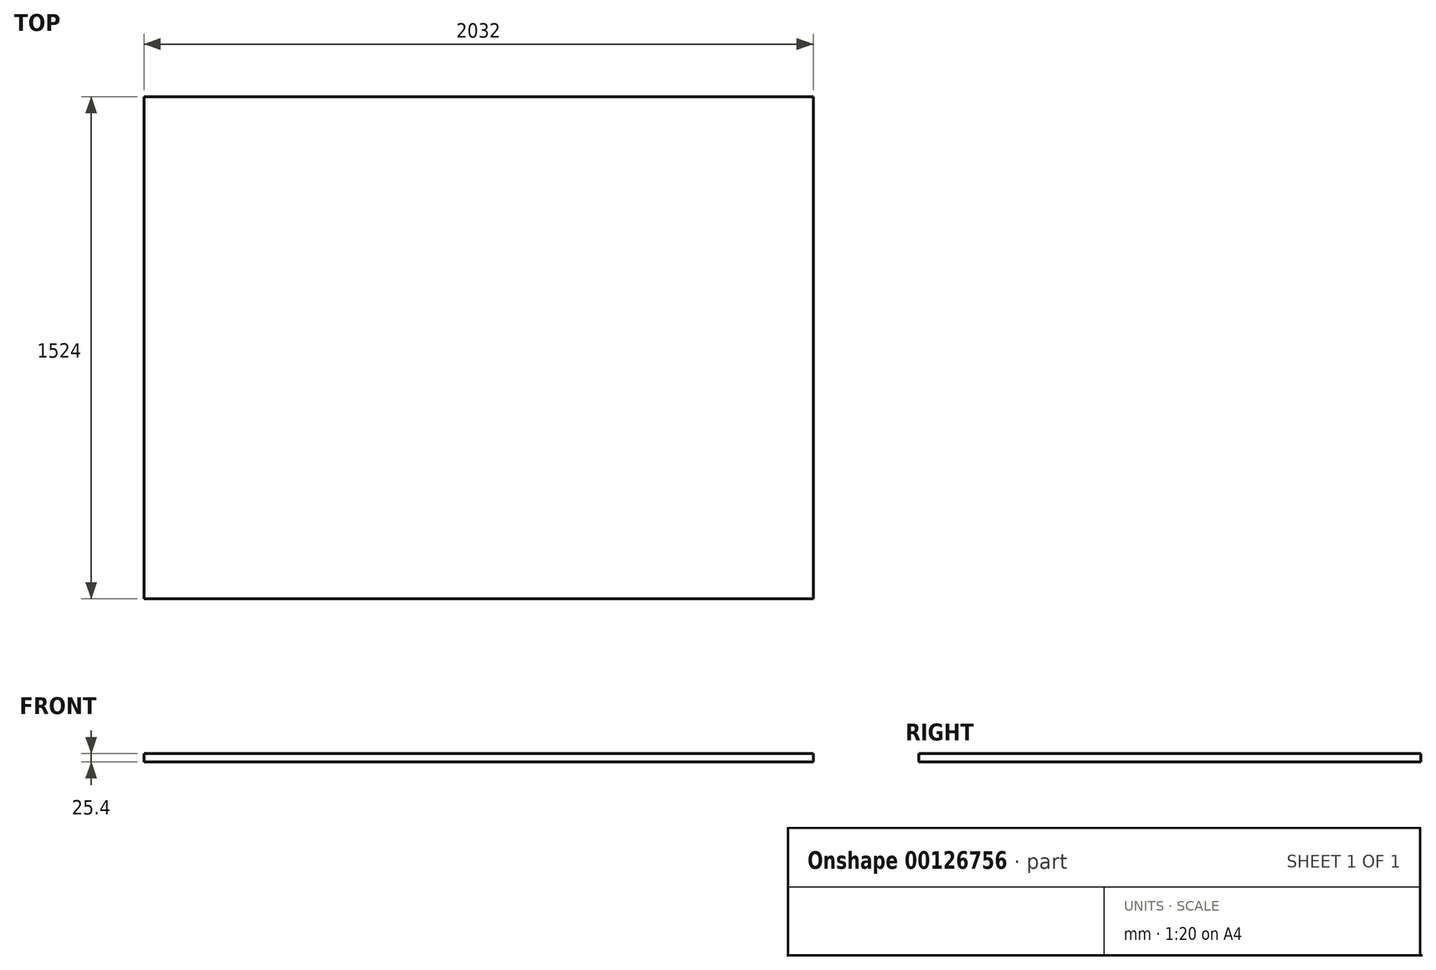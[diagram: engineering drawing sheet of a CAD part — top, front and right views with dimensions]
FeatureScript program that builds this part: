
annotation { "Feature Type Name" : "Feature", "Feature Type Description" : "" }
export const myFeature = defineFeature(function(context is Context, id is Id, definition is map)
    precondition{}
    {
        {
            var Q0;
            Q0=qCreatedBy(makeId("Top.planeOp"),FACE);
            var sketch = newSketch(context, id + "F0", { "sketchPlane" : qUnion([Q0])});
            skLineSegment(sketch, "E0.bottom", {"start": v(1016, 762) * mm, "end": v(-1016, 762) * mm});
            skLineSegment(sketch, "E0.top", {"start": v(1016, -762) * mm, "end": v(-1016, -762) * mm});
            skLineSegment(sketch, "E0.left", {"start": v(1016, 762) * mm, "end": v(1016, -762) * mm});
            skLineSegment(sketch, "E0.right", {"start": v(-1016, 762) * mm, "end": v(-1016, -762) * mm});
            skPoint(sketch, "E0.middle", {"position": v(0, 0) * mm});
            skSolve(sketch);
        }
        {
            var Q0;
            Q0 = qSketchRegion(id + "F0", true);
            extrude(context, id + "F1", {"entities" : qUnion([Q0]), "depth" : 25.4 * mm});
        }
    });
